# Revit family: Haworth_Patterns_Workwall_Systems
name_source: partatom
category: Furniture Systems
revit_build: Autodesk Revit 2018 (Build: 20170223_1515(x64)
units: mm (PartAtom-declared; Revit-internal decimal feet)

## family parameters
Always vertical = Yes
Cut with Voids When Loaded = No
OmniClass Number = 23.40.70.14.64.21
OmniClass Title = Systems Furniture
Part Type = Normal
Room Calculation Point = No
Round Connector Dimension = Use Diameter
Shared = No
Work Plane-Based = No

## types (6) — shared parameters
# of Backer Panel = 2
2 in. Credenza Thickness = No
Actual Credenza Height = 29 3/16"
Actual Depth = 22"
Actual Suspended Shelf 1 Height = 16"
Assembly Code = E2020200
Backer Finish = Haworth - Markerboard - White
Credenza Height = 30"
Credenza Top = No
Credenza Top Finish = Haworth _ Wood _ White Oak
Credenza Top Thickness = 1 3/16"
Description = Haworth - Patterns Workwall - Systems
Floor Support Shelf Door = No
Floor Supported Shelf = No
Floor Supported Shelf Finish = Haworth _ Wood _ White Oak
Full Tackboard = Yes
Manufacturer = Haworth
Max. Height = 60 1/2"
Max. Width = 126"
Min. Height = 44 1/2"
Min. Width = 78"
Model = Haworth - Patterns Workwall - Systems
Multi Sectional Backer = No
Partial Tackboard = No
Revision Number = 4
Shelf Finish = Haworth _ Wood _ White Oak
Shelf_1 = No
Shelf_2 = No
Shell Thickness = 3"
Size = Verify Final Dim. w/ Haworth
Sliding Door Finish = Haworth _ Wood _ White Oak
Stabalizer Panel Finish = Haworth _ Wood _ White Oak
Stabilizer Height = 25"
Standard Heights = 44 1/2, 60 1/2 in.
Standard Widths = 78, 102, 126 in.
Suspended Shelf 1 Backer = No
Suspended Shelf 1 Door = No
Suspended Shelf 1 Height = 16"
Suspended Shelf 2 Backer = No
Suspended Shelf 2 Door = No
Sustainability Info = http://www.haworth.com
Tackboard = No
Tackboard Finish = Haworth _ Fabric _ Tellure _ Ivory 3A-35
URL = https://www.haworth.com
URL - Product = https://www.haworth.com
Warranty = http://www.haworth.com
Workwall Backer = No
Workwall Shell Finish = Haworth _ Wood _ White Oak
zero-valued in all types: # of Shelves

## per-type parameters (varying)
| type | Actual Height | Actual Inside Width | Actual Width | Backer Height | Backer Width | Height | Max # of Shelves | Tackboard Height | Width |
| 102w 60 1/2h | 60 1/2" | 96" | 102" | 32 1/2" | 48" | 60 1/2" | 2 | 32" | 102" |
| 102w 44 1/2h | 44 1/2" | 96" | 102" | 16 1/2" | 48" | 44 1/2" | 1 | 16" | 102" |
| 78w 60 1/2h | 60 1/2" | 72" | 78" | 32 1/2" | 36" | 60 1/2" | 2 | 32" | 78" |
| 126w 60 1/2h | 60 1/2" | 120" | 126" | 32 1/2" | 60" | 60 1/2" | 2 | 32" | 126" |
| 78w 44 1/2h | 44 1/2" | 72" | 78" | 16 1/2" | 36" | 44 1/2" | 1 | 16" | 78" |
| 126w 44 1/2h | 44 1/2" | 120" | 126" | 16 1/2" | 60" | 44 1/2" | 1 | 16" | 126" |

## geometry (parser evidence)
native form markers: Blend x6, Sweep x30
no freeform markers — native parametric forms only
